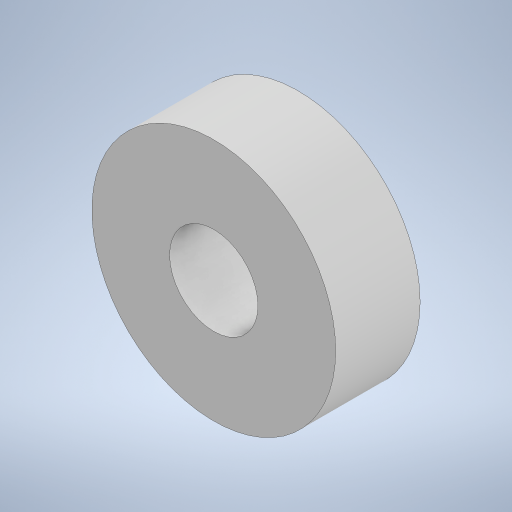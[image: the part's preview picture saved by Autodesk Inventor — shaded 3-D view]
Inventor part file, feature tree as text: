
AUTODESK INVENTOR PART (.ipt)
format: ipt  version: 2023 (Build 270158000, 158)  size: 210,944 bytes
history: native  units: in
note: dims shown in document units (in); Inventor stores cm internally (conversion verified against a paired STEP export)
features: extrude x1, sketch x1
ambient origin geometry x8: Origin, YZ Plane, XZ Plane, XY Plane, X Axis, Y Axis, Z Axis, Center Point
bodies: Solid1 (feature_tree)
feature tree (2):
  extrude  "Extrusion1"  Depth=0.3in
  sketch  "Sketch1"  dims[d0=0.314in d1=0.866in d2=0.3in d3=0.0in]
